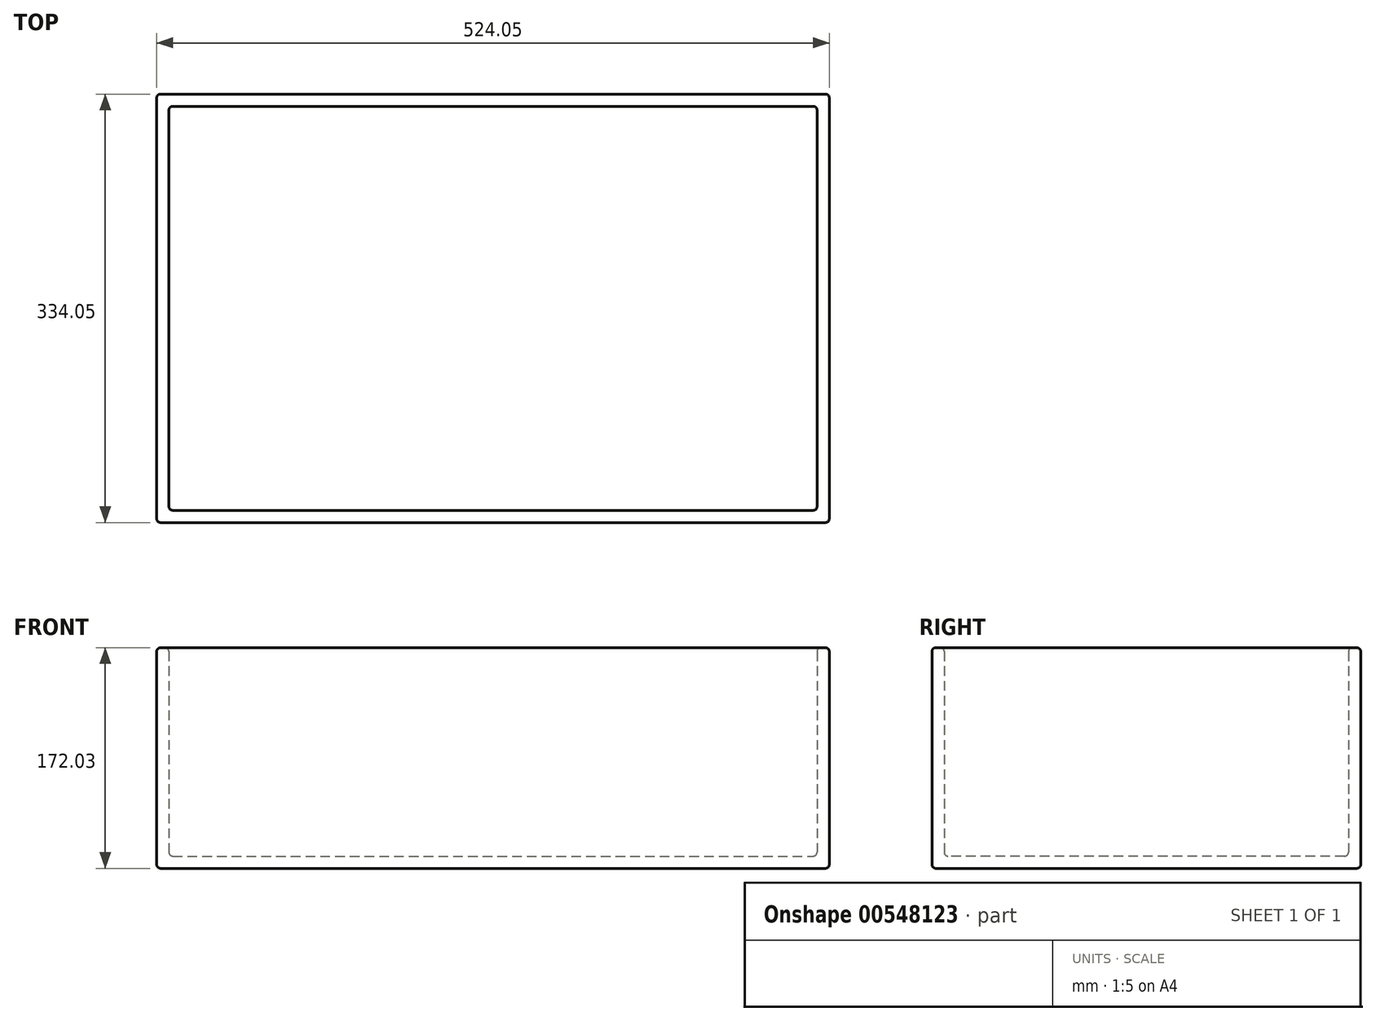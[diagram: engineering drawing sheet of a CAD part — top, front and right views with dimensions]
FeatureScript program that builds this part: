
annotation { "Feature Type Name" : "Feature", "Feature Type Description" : "" }
export const myFeature = defineFeature(function(context is Context, id is Id, definition is map)
    precondition{}
    {
        {
            var Q0;
            Q0=qCreatedBy(makeId("Top.planeOp"),FACE);
            var sketch = newSketch(context, id + "F0", { "sketchPlane" : qUnion([Q0])});
            skLineSegment(sketch, "E0.bottom", {"start": v(-213.81, 237.17) * mm, "end": v(310.24, 237.17) * mm});
            skLineSegment(sketch, "E0.top", {"start": v(-213.81, -96.88) * mm, "end": v(310.24, -96.88) * mm});
            skLineSegment(sketch, "E0.left", {"start": v(-213.81, 237.17) * mm, "end": v(-213.81, -96.88) * mm});
            skLineSegment(sketch, "E0.right", {"start": v(310.24, 237.17) * mm, "end": v(310.24, -96.88) * mm});
            skLineSegment(sketch, "E1.bottom", {"start": v(-204.29, 227.64) * mm, "end": v(300.71, 227.64) * mm});
            skLineSegment(sketch, "E1.top", {"start": v(-204.29, -87.36) * mm, "end": v(300.71, -87.36) * mm});
            skLineSegment(sketch, "E1.left", {"start": v(-204.29, 227.64) * mm, "end": v(-204.29, -87.36) * mm});
            skLineSegment(sketch, "E1.right", {"start": v(300.71, 227.64) * mm, "end": v(300.71, -87.36) * mm});
            skSolve(sketch);
        }
        {
            var Q0;
            Q0=makeQuery(id+"F0.imprint","IMPRINT",FACE,{"disambiguationData":[TD([[makeQuery(id+"F0.imprint","IMPRINT",EDGE,{"derivedFrom":sQuery(id+"F0.wireOp",EDGE,"E0.bottom")}),-1.0]])]});
            extrude(context, id + "F1", {"entities" : qUnion([Q0]), "depth" : 172.03 * mm, "offsetDistance" : 25 * mm});
        }
        {
            var Q0;
            Q0=makeQuery(id+"F0.imprint","IMPRINT",FACE,{"disambiguationData":[TD([[makeQuery(id+"F0.imprint","IMPRINT",EDGE,{"derivedFrom":sQuery(id+"F0.wireOp",EDGE,"E1.bottom")}),-1.0]])]});
            extrude(context, id + "F2", {"entities" : qUnion([Q0]), "operationType" : NewBodyOperationType.ADD, "depth" : 9.53 * mm, "offsetDistance" : 25 * mm});
        }
        {
            var Q0;
            Q0=makeQuery(id+"F1.opExtrude","SWEPT_FACE",FACE,{"disambiguationData":[OSD([sQuery(id+"F0.wireOp",EDGE,"E0.top")])]});
            var Q1;
            Q1=makeQuery(id+"F1.opExtrude","SWEPT_FACE",FACE,{"disambiguationData":[OSD([sQuery(id+"F0.wireOp",EDGE,"E0.right")])]});
            var Q2;
            Q2=makeQuery(id+"F1.opExtrude","SWEPT_FACE",FACE,{"disambiguationData":[OSD([sQuery(id+"F0.wireOp",EDGE,"E0.bottom")])]});
            var Q3;
            Q3=makeQuery(id+"F1.opExtrude","SWEPT_FACE",FACE,{"disambiguationData":[OSD([sQuery(id+"F0.wireOp",EDGE,"E0.left")])]});
            var Q4;
            Q4=makeQuery(id+"F1.opExtrude","CAP_FACE",FACE,{"disambiguationData":[OSD([sQuery(id+"F0.wireOp",EDGE,"E0.bottom"),sQuery(id+"F0.wireOp",EDGE,"E0.top"),sQuery(id+"F0.wireOp",EDGE,"E0.left"),sQuery(id+"F0.wireOp",EDGE,"E0.right"),sQuery(id+"F0.wireOp",EDGE,"E1.bottom"),sQuery(id+"F0.wireOp",EDGE,"E1.top"),sQuery(id+"F0.wireOp",EDGE,"E1.left"),sQuery(id+"F0.wireOp",EDGE,"E1.right")])],"isStart":false});
            var Q5;
            Q5=makeQuery(id+"F1.opExtrude","SWEPT_FACE",FACE,{"disambiguationData":[OSD([sQuery(id+"F0.wireOp",EDGE,"E1.left")])]});
            var Q6;
            Q6=makeQuery(id+"F1.opExtrude","SWEPT_FACE",FACE,{"disambiguationData":[OSD([sQuery(id+"F0.wireOp",EDGE,"E1.top")])]});
            var Q7;
            Q7=makeQuery(id+"F1.opExtrude","SWEPT_FACE",FACE,{"disambiguationData":[OSD([sQuery(id+"F0.wireOp",EDGE,"E1.right")])]});
            var Q8;
            Q8=makeQuery(id+"F1.opExtrude","SWEPT_FACE",FACE,{"disambiguationData":[OSD([sQuery(id+"F0.wireOp",EDGE,"E1.bottom")])]});
            var Q9;
            {var subQ0=sQuery(id+"F0.wireOp",EDGE,"E1.right");var subQ1=sQuery(id+"F0.wireOp",EDGE,"E1.left");var subQ2=sQuery(id+"F0.wireOp",EDGE,"E1.top");var subQ3=sQuery(id+"F0.wireOp",EDGE,"E1.bottom");Q9=makeQuery(id+"F2.boolean.opBoolean","MERGE",FACE,{"derivedFrom":[makeQuery(id+"F1.opExtrude","CAP_FACE",FACE,{"disambiguationData":[OSD([sQuery(id+"F0.wireOp",EDGE,"E0.bottom"),sQuery(id+"F0.wireOp",EDGE,"E0.top"),sQuery(id+"F0.wireOp",EDGE,"E0.left"),sQuery(id+"F0.wireOp",EDGE,"E0.right"),subQ3,subQ2,subQ1,subQ0])],"isStart":true}),makeQuery(id+"F2.opExtrude","CAP_FACE",FACE,{"disambiguationData":[OSD([subQ3,subQ2,subQ1,subQ0])],"isStart":true})]});}
            fillet(context, id + "F3", {"entities" : qUnion([Q0, Q1, Q2, Q3, Q4, Q5, Q6, Q7, Q8, Q9]), "radius" : 3 * mm, "tangentPropagation" : true, "allowEdgeOverflow" : false});
        }
    });
